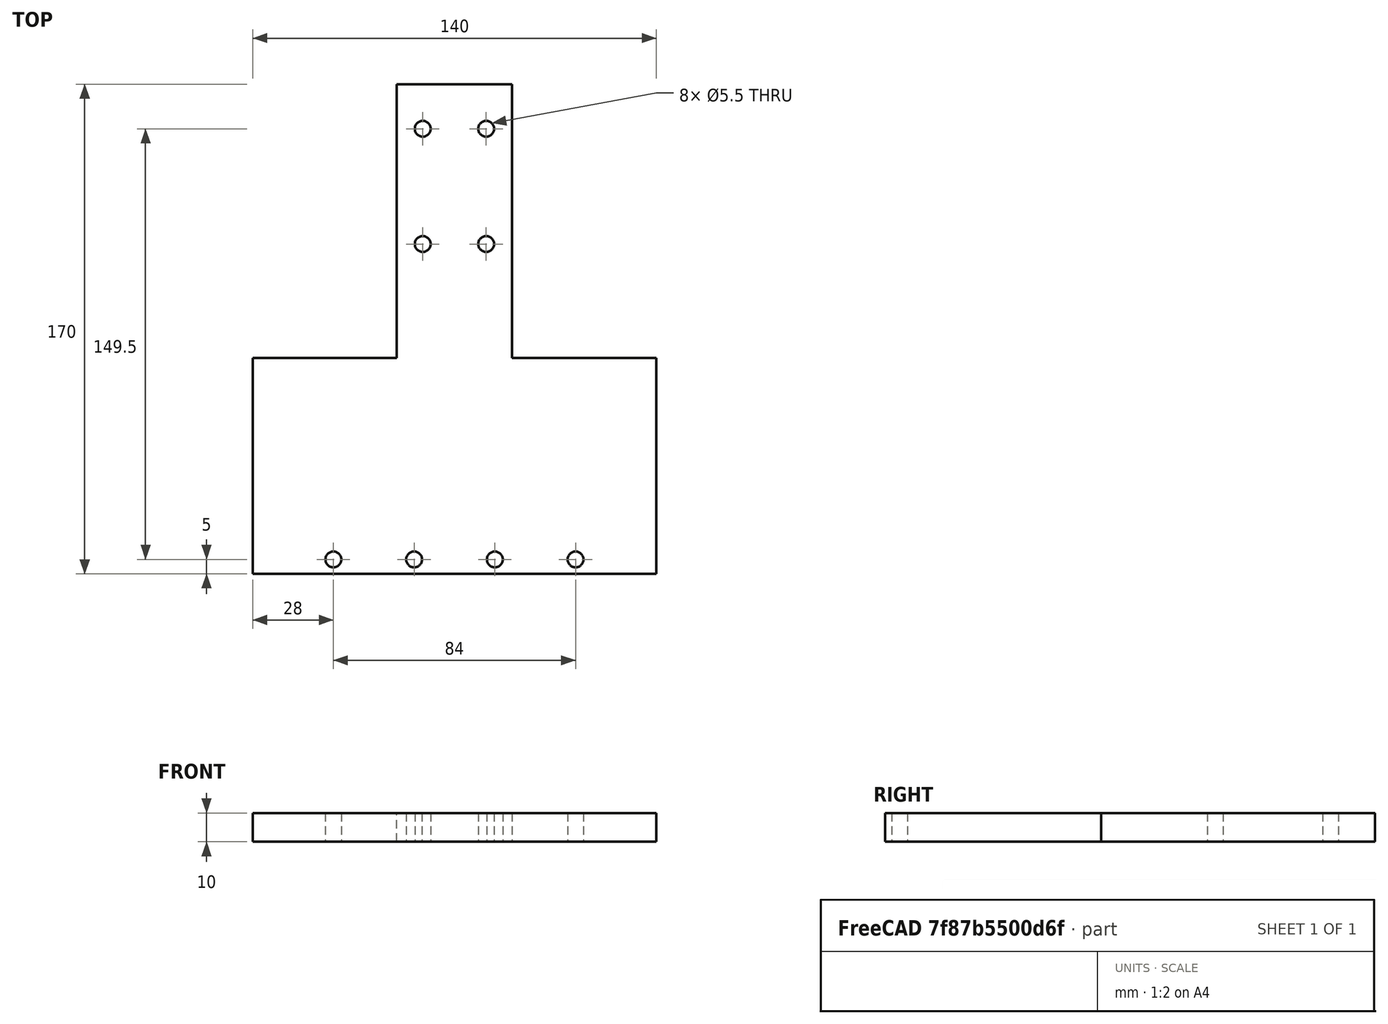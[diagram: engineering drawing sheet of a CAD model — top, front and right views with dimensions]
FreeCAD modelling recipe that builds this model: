
FCSTD DOCUMENT  (FreeCAD 0.17R13528 (Git))
Label: plate2
License: All rights reserved
LicenseURL: http://en.wikipedia.org/wiki/All_rights_reserved
objects: TechDraw::DrawViewDimension×26, Sketcher::SketchObject×5, PartDesign::Hole×3, PartDesign::LinearPattern×3, TechDraw::DrawProjGroupItem×3, PartDesign::Pad×2, PartDesign::Body×1, TechDraw::DrawSVGTemplate×1, TechDraw::DrawProjGroup×1, TechDraw::DrawViewAnnotation×1, TechDraw::DrawPage×1
note: 19 computed .brp shape members not serialized (recipe doc carries the construction recipe); baked Part::Feature solids carry a one-line shape summary decoded from their .brp

FEATURE [Sketcher::SketchObject] Sketch
  MapMode = 5
  Support = -> [XY_Plane]
  sketch-geometry (4):
    g0: LineSegment StartX=0 StartY=0 StartZ=0 EndX=140 EndY=0 EndZ=0
    g1: LineSegment StartX=140 StartY=0 StartZ=0 EndX=140 EndY=75 EndZ=0
    g2: LineSegment StartX=140 StartY=75 StartZ=0 EndX=0 EndY=75 EndZ=0
    g3: LineSegment StartX=0 StartY=75 StartZ=0 EndX=0 EndY=0 EndZ=0
  constraints (11):
    c: Coincident(g0,g1)
    c: Coincident(g1,g2)
    c: Coincident(g2,g3)
    c: Coincident(g3,g0)
    c: Horizontal(g0)
    c: Horizontal(g2)
    c: Vertical(g1)
    c: Vertical(g3)
    c: Coincident(g0,g-1)
    c: DistanceX(g0,g0) = 140
    c: DistanceY(g3,g3) = 75
FEATURE [PartDesign::Pad] Pad
  Length = 10
  Length2 = 100
  Profile = -> Sketch
  Type = 0
FEATURE [Sketcher::SketchObject] Sketch001
  MapMode = 5
  Placement = pos=(0,75,0) rot=(0,0.707107,0.707107;3.14159rad)
  Support = -> [Pad]
  sketch-geometry (4):
    g0: LineSegment StartX=-90 StartY=0 StartZ=0 EndX=-50 EndY=0 EndZ=0
    g1: LineSegment StartX=-50 StartY=0 StartZ=0 EndX=-50 EndY=10 EndZ=0
    g2: LineSegment StartX=-50 StartY=10 StartZ=0 EndX=-90 EndY=10 EndZ=0
    g3: LineSegment StartX=-90 StartY=10 StartZ=0 EndX=-90 EndY=0 EndZ=0
  constraints (12):
    c: Coincident(g0,g1)
    c: Coincident(g1,g2)
    c: Coincident(g2,g3)
    c: Coincident(g3,g0)
    c: Horizontal(g0)
    c: Horizontal(g2)
    c: Vertical(g1)
    c: Vertical(g3)
    c: PointOnObject(g0,g-1)
    c: DistanceX(g2,g2) = 40
    c: DistanceY(g1,g1) = 10
    c: DistanceX(g0,g-1) = 50
FEATURE [PartDesign::Pad] Pad001
  BaseFeature = -> Pad
  Length = 95
  Length2 = 100
  Profile = -> Sketch001
  Type = 0
FEATURE [Sketcher::SketchObject] Sketch002
  MapMode = 5
  Placement = pos=(0,0,10) rot=(0,0,1;0rad)
  Support = -> [Pad001]
  sketch-geometry (1):
    g0: Circle CenterX=28 CenterY=5 CenterZ=0 NormalX=0 NormalY=0 NormalZ=1 AngleXU=0 Radius=5.81966
  constraints (2):
    c: Distance(g0,g-2) = 28
    c: Distance(g0,g-1) = 5
FEATURE [PartDesign::Hole] Hole
  BaseFeature = -> Pad001
  Depth = 25
  DepthType = 1
  Diameter = 5.5
  DrillPoint = 0
  DrillPointAngle = 118
  HoleCutCountersinkAngle = 90
  HoleCutDepth = 0
  HoleCutDiameter = 5
  HoleCutType = 0
  ModelActualThread = false
  Profile = -> Sketch002
  Tapered = false
  TaperedAngle = 90
  ThreadAngle = 0
  ThreadClass = 0
  ThreadCutOffInner = 0
  ThreadCutOffOuter = 0
  ThreadDirection = 0
  ThreadFit = 0
  ThreadPitch = 0
  ThreadSize = 6
  ThreadType = 1
  Threaded = false
FEATURE [PartDesign::LinearPattern] LinearPattern
  BaseFeature = -> Hole
  Direction = -> Sketch002 [H_Axis]
  Length = 84
  Occurrences = 4
  Originals = -> [Hole]
FEATURE [Sketcher::SketchObject] Sketch003
  MapMode = 5
  Placement = pos=(0,0,10) rot=(0,0,1;0rad)
  Support = -> [LinearPattern]
  sketch-geometry (1):
    g0: Circle CenterX=59 CenterY=114.5 CenterZ=0 NormalX=0 NormalY=0 NormalZ=1 AngleXU=0 Radius=6.2774
  constraints (2):
    c: Distance(g0,g-1) = 114.5
    c: Distance(g0,g-2) = 59
FEATURE [PartDesign::Hole] Hole001
  BaseFeature = -> LinearPattern
  Depth = 25
  DepthType = 1
  Diameter = 5.5
  DrillPoint = 0
  DrillPointAngle = 118
  HoleCutCountersinkAngle = 90
  HoleCutDepth = 0
  HoleCutDiameter = 5
  HoleCutType = 0
  ModelActualThread = false
  Profile = -> Sketch003
  Tapered = false
  TaperedAngle = 90
  ThreadAngle = 0
  ThreadClass = 0
  ThreadCutOffInner = 0
  ThreadCutOffOuter = 0
  ThreadDirection = 0
  ThreadFit = 0
  ThreadPitch = 0
  ThreadSize = 6
  ThreadType = 1
  Threaded = false
FEATURE [PartDesign::LinearPattern] LinearPattern001
  BaseFeature = -> Hole001
  Direction = -> Sketch003 [H_Axis]
  Length = 22
  Occurrences = 2
  Originals = -> [Hole001]
FEATURE [PartDesign::LinearPattern] LinearPattern002
  BaseFeature = -> LinearPattern001
  Direction = -> Sketch003 [V_Axis]
  Length = 40
  Occurrences = 2
  Originals = -> [Hole001]
FEATURE [Sketcher::SketchObject] Sketch004
  MapMode = 5
  Placement = pos=(0,0,10) rot=(0,0,1;0rad)
  Support = -> [LinearPattern002]
  sketch-geometry (1):
    g0: Circle CenterX=81 CenterY=154.5 CenterZ=0 NormalX=0 NormalY=0 NormalZ=1 AngleXU=0 Radius=4.22708
  constraints (2):
    c: Distance(g0,g-1) = 154.5
    c: Distance(g0,g-2) = 81
FEATURE [PartDesign::Hole] Hole002
  BaseFeature = -> LinearPattern002
  Depth = 25
  DepthType = 1
  Diameter = 5.5
  DrillPoint = 0
  DrillPointAngle = 118
  HoleCutCountersinkAngle = 90
  HoleCutDepth = 0
  HoleCutDiameter = 5
  HoleCutType = 0
  ModelActualThread = false
  Profile = -> Sketch004
  Tapered = false
  TaperedAngle = 90
  ThreadAngle = 0
  ThreadClass = 0
  ThreadCutOffInner = 0
  ThreadCutOffOuter = 0
  ThreadDirection = 0
  ThreadFit = 0
  ThreadPitch = 0
  ThreadSize = 6
  ThreadType = 1
  Threaded = false
FEATURE [PartDesign::Body] Body
  Group = -> [Sketch,Pad,Sketch001,Pad001,Sketch002,Hole,LinearPattern,Sketch003,Hole001,LinearPattern001,LinearPattern002,Sketch004,Hole002]
  Origin = -> Origin
  Tip = -> Hole002
FEATURE [TechDraw::DrawSVGTemplate] Template
  EditableTexts = Designed_by_Name=Lukas Winter; FC-Date=27.08.2018; FC-SC=1:2; FC-SH=1/1; FC-Title=COSI Measure v1.0; Subtitle=Mechanical assembly - plate 2
  Height = 210
  Orientation = 1
  Width = 297
FEATURE [TechDraw::DrawProjGroupItem] ProjItem  label="Front"
  CoarseView = false
  Direction = (0,-1,0)
  Focus = 100
  HardHidden = false
  IsoCount = 0
  IsoHidden = false
  IsoVisible = false
  LockPosition = false
  Perspective = false
  Rotation = 0
  RotationVector = (1,0,0)
  ScaleType = 0
  SeamHidden = false
  SeamVisible = false
  SmoothHidden = false
  SmoothVisible = false
  Source = -> [Body]
  Type = 0
  X = -100
  Y = 0
FEATURE [TechDraw::DrawProjGroupItem] ProjItem001  label="Left"
  CoarseView = false
  Direction = (-1,0,0)
  Focus = 100
  HardHidden = false
  IsoCount = 0
  IsoHidden = false
  IsoVisible = false
  LockPosition = false
  Perspective = false
  Rotation = 0
  RotationVector = (0,1,0)
  ScaleType = 0
  SeamHidden = false
  SeamVisible = false
  SmoothHidden = false
  SmoothVisible = false
  Source = -> [Body]
  Type = 1
  X = 100
  Y = 0
FEATURE [TechDraw::DrawProjGroupItem] ProjItem002  label="Top"
  CoarseView = false
  Direction = (0,0,1)
  Focus = 100
  HardHidden = false
  IsoCount = 0
  IsoHidden = false
  IsoVisible = false
  LockPosition = false
  Perspective = false
  Rotation = 0
  RotationVector = (1,0,0)
  ScaleType = 0
  SeamHidden = false
  SeamVisible = false
  SmoothHidden = false
  SmoothVisible = false
  Source = -> [Body]
  Type = 4
  X = 0
  Y = -100
FEATURE [TechDraw::DrawProjGroup] ProjGroup
  Anchor = -> ProjItem
  AutoDistribute = true
  CubeDirs = (1) [(0,0,0)]
  CubeRotations = (1) [(0,0,0)]
  LockPosition = false
  ProjectionType = 0
  Rotation = 0
  Scale = 0.5
  ScaleType = 2
  Source = -> [Body]
  Views = -> [ProjItem,ProjItem001,ProjItem002]
  X = 80.5165
  Y = 179.775
  spacingX = 15
  spacingY = 15
FEATURE [TechDraw::DrawViewDimension] Dimension
  FormatSpec = %.2f
  LockPosition = false
  MeasureType = 1
  References2D = -> [ProjItem002]
  Rotation = 0
  ScaleType = 0
  Type = 2
  X = -54.8943
  Y = -29.5838
FEATURE [TechDraw::DrawViewDimension] Dimension001
  FormatSpec = %.2f
  LockPosition = false
  MeasureType = 1
  References2D = -> [ProjItem002]
  Rotation = 0
  ScaleType = 0
  Type = 1
  X = -11.6692
  Y = -55.8805
FEATURE [TechDraw::DrawViewDimension] Dimension002
  FormatSpec = %.2f
  LockPosition = false
  MeasureType = 1
  References2D = -> [ProjItem002]
  Rotation = 0
  ScaleType = 0
  Type = 1
  X = 2.84004
  Y = -30.2938
FEATURE [TechDraw::DrawViewDimension] Dimension003
  FormatSpec = %.2f
  LockPosition = false
  MeasureType = 1
  References2D = -> [ProjItem002]
  Rotation = 0
  ScaleType = 0
  Type = 1
  X = 16.3302
  Y = -59.8776
FEATURE [TechDraw::DrawViewDimension] Dimension004
  FormatSpec = %.2f
  LockPosition = false
  MeasureType = 1
  References2D = -> [ProjItem002]
  Rotation = 0
  ScaleType = 0
  Type = 1
  X = 30.2938
  Y = -24.1404
FEATURE [TechDraw::DrawViewDimension] Dimension005
  FormatSpec = %.2f
  LockPosition = false
  MeasureType = 1
  References2D = -> [ProjItem002]
  Rotation = 0
  ScaleType = 0
  Type = 1
  X = -24.1404
  Y = -27.4537
FEATURE [TechDraw::DrawViewDimension] Dimension006
  FormatSpec = %.2f
  LockPosition = false
  MeasureType = 1
  References2D = -> [ProjItem002]
  Rotation = 0
  ScaleType = 0
  Type = 5
  X = 3.07671
  Y = -16.3302
FEATURE [TechDraw::DrawViewDimension] Dimension007
  FormatSpec = %.2f
  LockPosition = false
  MeasureType = 1
  References2D = -> [ProjItem002]
  Rotation = 0
  ScaleType = 0
  Type = 5
  X = 3.07671
  Y = -16.3302
FEATURE [TechDraw::DrawViewDimension] Dimension009
  FormatSpec = %.2f
  LockPosition = false
  MeasureType = 1
  References2D = -> [ProjItem002]
  Rotation = 0
  ScaleType = 0
  Type = 5
  X = 3.01121
  Y = -16.3222
FEATURE [TechDraw::DrawViewDimension] Dimension010
  FormatSpec = %.2f
  LockPosition = false
  MeasureType = 1
  References2D = -> [ProjItem002]
  Rotation = 0
  ScaleType = 0
  Type = 5
  X = 0
  Y = 0
FEATURE [TechDraw::DrawViewDimension] Dimension011
  FormatSpec = %.2f
  LockPosition = false
  MeasureType = 1
  References2D = -> [ProjItem002]
  Rotation = 0
  ScaleType = 0
  Type = 5
  X = 0
  Y = 0
FEATURE [TechDraw::DrawViewDimension] Dimension012
  FormatSpec = %.2f
  LockPosition = false
  MeasureType = 1
  References2D = -> [ProjItem002]
  Rotation = 0
  ScaleType = 0
  Type = 5
  X = -33.5283
  Y = 54.4342
FEATURE [TechDraw::DrawViewDimension] Dimension013
  FormatSpec = %.2f
  LockPosition = false
  MeasureType = 1
  References2D = -> [ProjItem002]
  Rotation = 0
  ScaleType = 0
  Type = 5
  X = 37.2756
  Y = 53.8425
FEATURE [TechDraw::DrawViewDimension] Dimension014
  FormatSpec = %.2f
  LockPosition = false
  MeasureType = 1
  References2D = -> [ProjItem002]
  Rotation = 0
  ScaleType = 0
  Type = 1
  X = 3.9445
  Y = 64.2954
FEATURE [TechDraw::DrawViewDimension] Dimension015
  FormatSpec = %.2f
  LockPosition = false
  MeasureType = 1
  References2D = -> [ProjItem002]
  Rotation = 0
  ScaleType = 0
  Type = 1
  X = -19.3281
  Y = 30.7671
FEATURE [TechDraw::DrawViewDimension] Dimension016
  FormatSpec = %.2f
  LockPosition = false
  MeasureType = 1
  References2D = -> [ProjItem002]
  Rotation = 0
  ScaleType = 0
  Type = 1
  X = 23.667
  Y = 32.3449
FEATURE [TechDraw::DrawViewDimension] Dimension017
  FormatSpec = %.2f
  LockPosition = false
  MeasureType = 1
  References2D = -> [ProjItem002]
  Rotation = 0
  ScaleType = 0
  Type = 2
  X = 50.3443
  Y = 25.1104
FEATURE [TechDraw::DrawViewDimension] Dimension018
  FormatSpec = %.2f
  LockPosition = false
  MeasureType = 1
  References2D = -> [ProjItem002]
  Rotation = 0
  ScaleType = 0
  Type = 2
  X = 39.6837
  Y = 40.3485
FEATURE [TechDraw::DrawViewDimension] Dimension020
  FormatSpec = %.2f
  LockPosition = false
  MeasureType = 1
  References2D = -> [ProjItem002]
  Rotation = 0
  ScaleType = 0
  Type = 2
  X = 53.6453
  Y = -24.4559
FEATURE [TechDraw::DrawViewDimension] Dimension021
  FormatSpec = %.2f
  LockPosition = false
  MeasureType = 1
  References2D = -> [ProjItem]
  Rotation = 0
  ScaleType = 0
  Type = 1
  X = 0.197225
  Y = 12.0307
FEATURE [TechDraw::DrawViewDimension] Dimension022
  FormatSpec = %.2f
  LockPosition = false
  MeasureType = 1
  References2D = -> [ProjItem001]
  Rotation = 0
  ScaleType = 0
  Type = 2
  X = 52.8564
  Y = -13.6085
FEATURE [TechDraw::DrawViewDimension] Dimension023
  FormatSpec = %.2f
  LockPosition = false
  MeasureType = 1
  References2D = -> [ProjItem001]
  Rotation = 0
  ScaleType = 0
  Type = 1
  X = -22.037
  Y = 11.8827
FEATURE [TechDraw::DrawViewDimension] Dimension024
  FormatSpec = %.2f
  LockPosition = false
  MeasureType = 1
  References2D = -> [ProjItem001]
  Rotation = 0
  ScaleType = 0
  Type = 1
  X = 21.821
  Y = 12.0988
FEATURE [TechDraw::DrawViewDimension] Dimension025
  FormatSpec = %.2f
  LockPosition = false
  MeasureType = 1
  References2D = -> [ProjItem002]
  Rotation = 0
  ScaleType = 0
  Type = 1
  X = 3.24074
  Y = -75.4012
FEATURE [TechDraw::DrawViewDimension] Dimension026
  FormatSpec = %.2f
  LockPosition = false
  MeasureType = 1
  References2D = -> [ProjItem002]
  Rotation = 0
  ScaleType = 0
  Type = 1
  X = -21.3008
  Y = 7.5674
FEATURE [TechDraw::DrawViewDimension] Dimension027
  FormatSpec = %.2f
  LockPosition = false
  MeasureType = 1
  References2D = -> [ProjItem002]
  Rotation = 0
  ScaleType = 0
  Type = 1
  X = 24.9444
  Y = 7.84767
FEATURE [TechDraw::DrawViewAnnotation] Annotation
  Font = osifont
  LineSpace = 80
  LockPosition = false
  MaxWidth = -1
  Rotation = 0
  ScaleType = 0
  Text = Optional: Make a countersink in the  | d=5.5mm holes.
  TextSize = 4
  TextStyle = 0
  X = 245.032
  Y = 67.8222
FEATURE [TechDraw::DrawPage] Page
  KeepUpdated = true
  ProjectionType = 0
  Template = -> Template
  Views = -> [ProjGroup,Dimension,Dimension001,Dimension002,Dimension003,Dimension004,Dimension005,Dimension006,Dimension007,Dimension009,Dimension010,Dimension011,Dimension012,Dimension013,Dimension014,Dimension015,Dimension016,Dimension017,Dimension018,Dimension020,Dimension021,Dimension022,Dimension023,Dimension024,Dimension025,Dimension026,Dimension027,Annotation]
